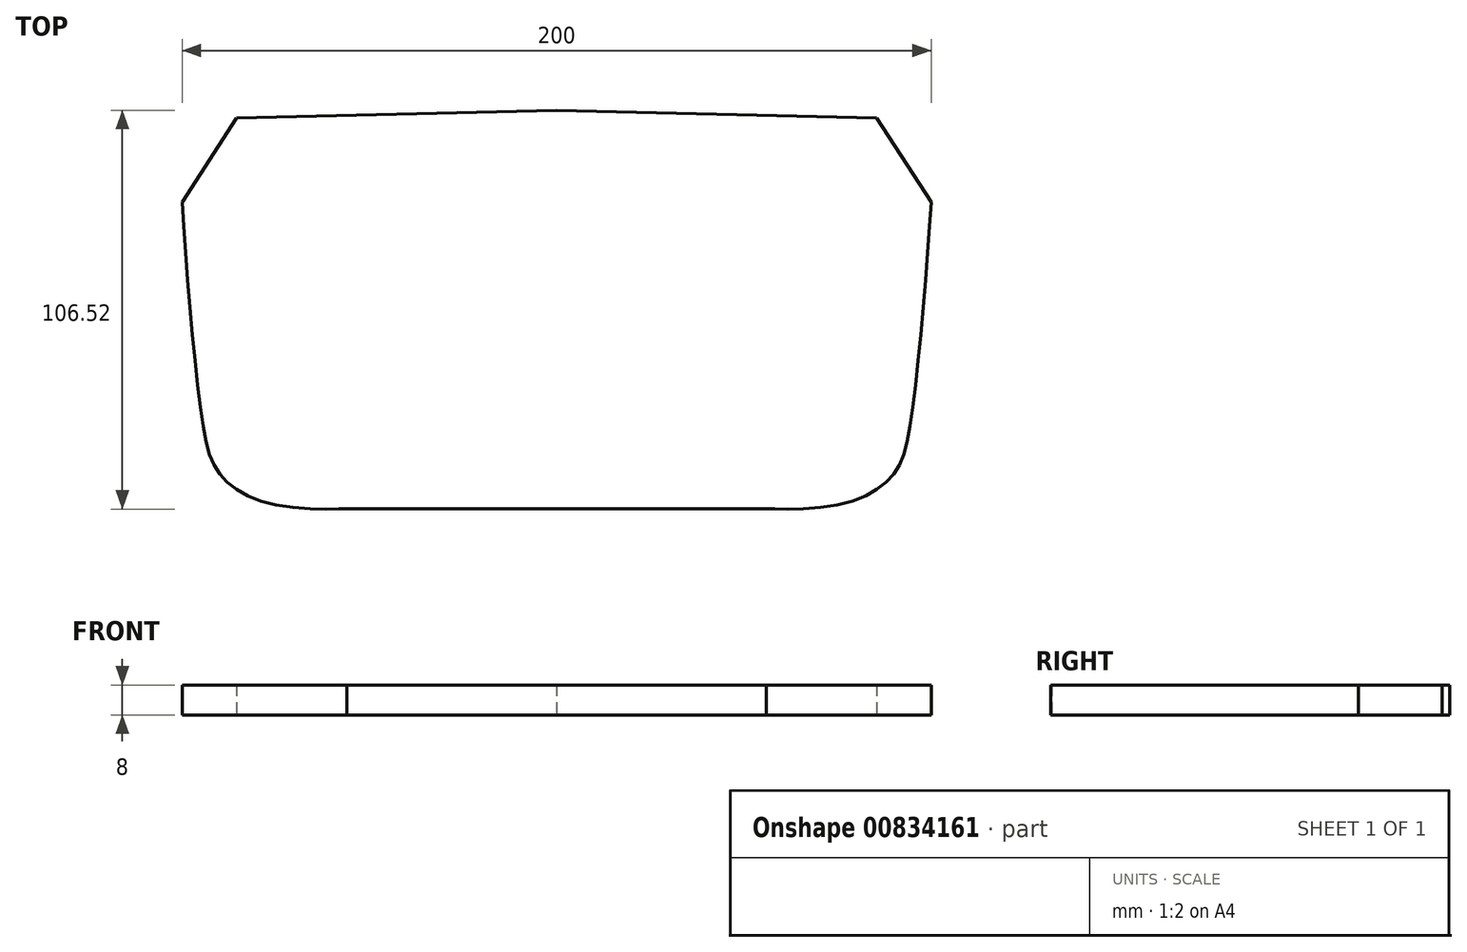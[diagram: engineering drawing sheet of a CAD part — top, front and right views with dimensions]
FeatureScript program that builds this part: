
annotation { "Feature Type Name" : "Feature", "Feature Type Description" : "" }
export const myFeature = defineFeature(function(context is Context, id is Id, definition is map)
    precondition{}
    {
        {
            var Q0;
            Q0=qCreatedBy(makeId("Top.planeOp"),FACE);
            var sketch = newSketch(context, id + "F0", { "sketchPlane" : qUnion([Q0])});
            skFitSpline(sketch, "E0", {"points": [v(-55.98, -49.44) * mm, v(-75.03, -48.4) * mm, v(-89.35, -41.01) * mm, v(-94.43, -26.88) * mm, v(-100, 32.5) * mm], "startDerivative": vector(-34.38, -2.46) * mm, "endDerivative": vector(-9.03, 144.89) * mm});
            skLineSegment(sketch, "E1", {"start": v(-100, 32.5) * mm, "end": v(-85.48, 54.87) * mm});
            skLineSegment(sketch, "E2", {"start": v(-85.48, 54.87) * mm, "end": v(0, 56.95) * mm});
            skLineSegment(sketch, "E3", {"start": v(-55.98, -49.44) * mm, "end": v(0, -49.44) * mm});
            skFitSpline(sketch, "E4.MirrorCS", {"points": [v(55.98, -49.44) * mm, v(75.03, -48.4) * mm, v(89.35, -41.01) * mm, v(94.43, -26.88) * mm, v(100, 32.5) * mm], "startDerivative": vector(34.38, -2.46) * mm, "endDerivative": vector(9.03, 144.89) * mm});
            skPoint(sketch, "E5.MirrorP", {"position": v(0, 0) * mm});
            skLineSegment(sketch, "E6.MirrorCS", {"start": v(100, 32.5) * mm, "end": v(85.48, 54.87) * mm});
            skLineSegment(sketch, "E7.MirrorCS", {"start": v(55.98, -49.44) * mm, "end": v(0, -49.44) * mm});
            skLineSegment(sketch, "E8.MirrorCS", {"start": v(85.48, 54.87) * mm, "end": v(0, 56.95) * mm});
            skSolve(sketch);
        }
        {
            var Q0;
            Q0=makeQuery(id+"F0.imprint","IMPRINT",FACE,{"disambiguationData":[TD([[makeQuery(id+"F0.imprint","IMPRINT",EDGE,{"derivedFrom":sQuery(id+"F0.wireOp",EDGE,"E0")}),-1.0]])]});
            extrude(context, id + "F1", {"entities" : qUnion([Q0]), "depth" : 8 * mm, "offsetDistance" : 25 * mm});
        }
    });
